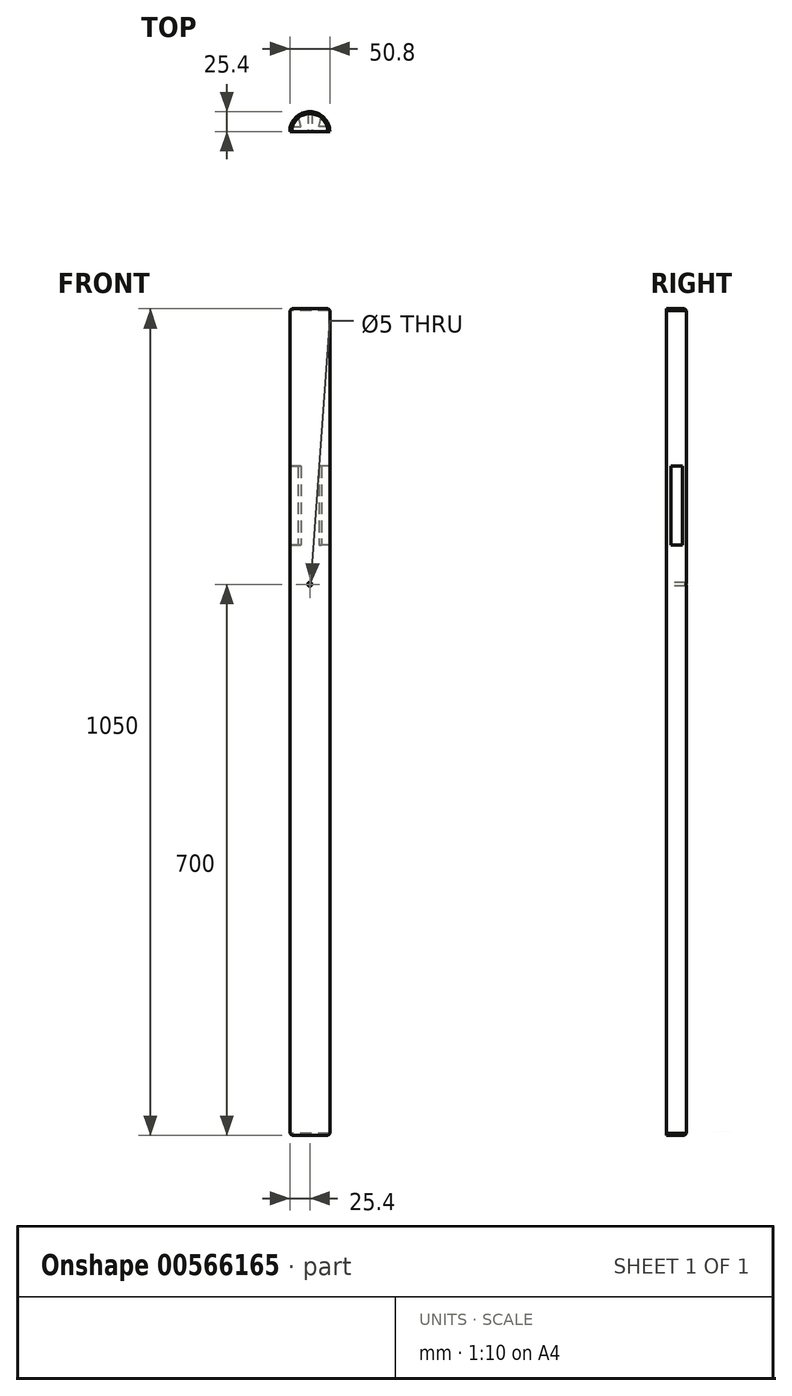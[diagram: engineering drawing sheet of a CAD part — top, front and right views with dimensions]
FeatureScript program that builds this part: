
annotation { "Feature Type Name" : "Feature", "Feature Type Description" : "" }
export const myFeature = defineFeature(function(context is Context, id is Id, definition is map)
    precondition{}
    {
        {
            var Q0;
            Q0=qCreatedBy(makeId("Top.planeOp"),FACE);
            var sketch = newSketch(context, id + "F0", { "sketchPlane" : qUnion([Q0])});
            skArc(sketch, "E0", {"start": v(25.4, 0) * mm, "mid": v(0, 25.4) * mm, "end": v(-25.4, 0) * mm});
            skLineSegment(sketch, "E1", {"start": v(-25.4, 0) * mm, "end": v(25.4, 0) * mm});
            skLineSegment(sketch, "E2", {"start": v(0, 0) * mm, "end": v(0, 25.4) * mm, "construction": true});
            skSolve(sketch);
        }
        {
            var Q0;
            Q0=qCreatedBy(makeId("Top.planeOp"),FACE);
            var sketch = newSketch(context, id + "F1", { "sketchPlane" : qUnion([Q0])});
            skArc(sketch, "E3", {"start": v(25.4, 0) * mm, "mid": v(25.21, 3.06) * mm, "end": v(24.66, 6.08) * mm});
            skLineSegment(sketch, "E4", {"start": v(-25.4, 0) * mm, "end": v(25.4, 0) * mm});
            skLineSegment(sketch, "E5", {"start": v(-24.66, 6.08) * mm, "end": v(-11.4, 6.08) * mm});
            skLineSegment(sketch, "E6", {"start": v(-11.4, 6.08) * mm, "end": v(-14.88, 20.59) * mm});
            skLineSegment(sketch, "E7.MirrorCS", {"start": v(11.4, 6.08) * mm, "end": v(14.88, 20.59) * mm});
            skLineSegment(sketch, "E8.MirrorCS", {"start": v(24.66, 6.08) * mm, "end": v(11.4, 6.08) * mm});
            skArc(sketch, "E9.trimOffspring", {"start": v(-24.66, 6.08) * mm, "mid": v(-25.21, 3.06) * mm, "end": v(-25.4, 0) * mm});
            skArc(sketch, "E10.trimOffspring", {"start": v(14.88, 20.59) * mm, "mid": v(0, 25.4) * mm, "end": v(-14.88, 20.59) * mm});
            skSolve(sketch);
        }
        {
            var Q0;
            Q0 = qSketchRegion(id + "F0", true);
            extrude(context, id + "F2", {"entities" : qUnion([Q0]), "oppositeDirection" : true, "depth" : 750 * mm, "offsetDistance" : 25.4 * mm});
        }
        {
            var Q0;
            Q0 = qSketchRegion(id + "F1", true);
            extrude(context, id + "F3", {"entities" : qUnion([Q0]), "operationType" : NewBodyOperationType.ADD, "depth" : 100 * mm, "offsetDistance" : 25.4 * mm});
        }
        {
            var Q0;
            Q0=qCreatedBy(makeId("Top.planeOp"),FACE);
            var sketch = newSketch(context, id + "F4", { "sketchPlane" : qUnion([Q0])});
            skArc(sketch, "E11", {"start": v(25.4, 0) * mm, "mid": v(0, 25.4) * mm, "end": v(-25.4, 0) * mm});
            skLineSegment(sketch, "E12", {"start": v(-25.4, 0) * mm, "end": v(25.4, 0) * mm});
            skSolve(sketch);
        }
        {
            var Q0;
            Q0=makeQuery(id+"F4.imprint","IMPRINT",FACE,{"disambiguationData":[TD([[makeQuery(id+"F4.imprint","IMPRINT",EDGE,{"derivedFrom":sQuery(id+"F4.wireOp",EDGE,"E11")}),1.0]])]});
            extrude(context, id + "F5", {"entities" : qUnion([Q0]), "operationType" : NewBodyOperationType.ADD, "depth" : 300 * mm, "offsetDistance" : 25.4 * mm, "hasSecondDirection" : true, "secondDirectionOppositeDirection" : false, "secondDirectionDepth" : 100 * mm});
        }
        {
            var Q0;
            Q0=makeQuery(id+"F2.opExtrude","CAP_EDGE",EDGE,{"disambiguationData":[OSD([sQuery(id+"F0.wireOp",EDGE,"E0")])],"isStart":false});
            chamfer(context, id + "F6", {"entities" : qUnion([Q0]), "width" : 2.54 * mm, "tangentPropagation" : true});
        }
        {
            var Q0;
            Q0=makeQuery(id+"F5.opExtrude","CAP_EDGE",EDGE,{"disambiguationData":[OSD([sQuery(id+"F4.wireOp",EDGE,"E11")])],"isStart":false});
            chamfer(context, id + "F7", {"entities" : qUnion([Q0]), "width" : 2.54 * mm, "tangentPropagation" : true});
        }
        {
            var Q0;
            Q0=qCreatedBy(makeId("Front.planeOp"),FACE);
            var sketch = newSketch(context, id + "F8", { "sketchPlane" : qUnion([Q0])});
            skLineSegment(sketch, "E13", {"start": v(0, 0) * mm, "end": v(0, -2.5) * mm});
            skCircle(sketch, "E14", {"center": v(0, -50) * mm, "radius": 2.5 * mm});
            skSolve(sketch);
        }
        {
            var Q0;
            Q0=sQuery(id+"F8.wireOp",VERTEX,"E14.center");
            var Q1;
            Q1=makeQuery(id+"F2.opExtrude","SWEPT_BODY",BODY,{"disambiguationData":[OSD([sQuery(id+"F0.wireOp",EDGE,"E0"),sQuery(id+"F0.wireOp",EDGE,"E1")])]});
            hole(context, id + "F9", {"style" : HoleStyle.SIMPLE, "endStyle" : HoleEndStyle.THROUGH, "holeDiameter" : 5 * mm, "isTappedThrough" : true, "tappedDepth" : 12 * mm, "tapClearance" : 3, "locations" : qUnion([Q0]), "scope" : qUnion([Q1])});
        }
    });
